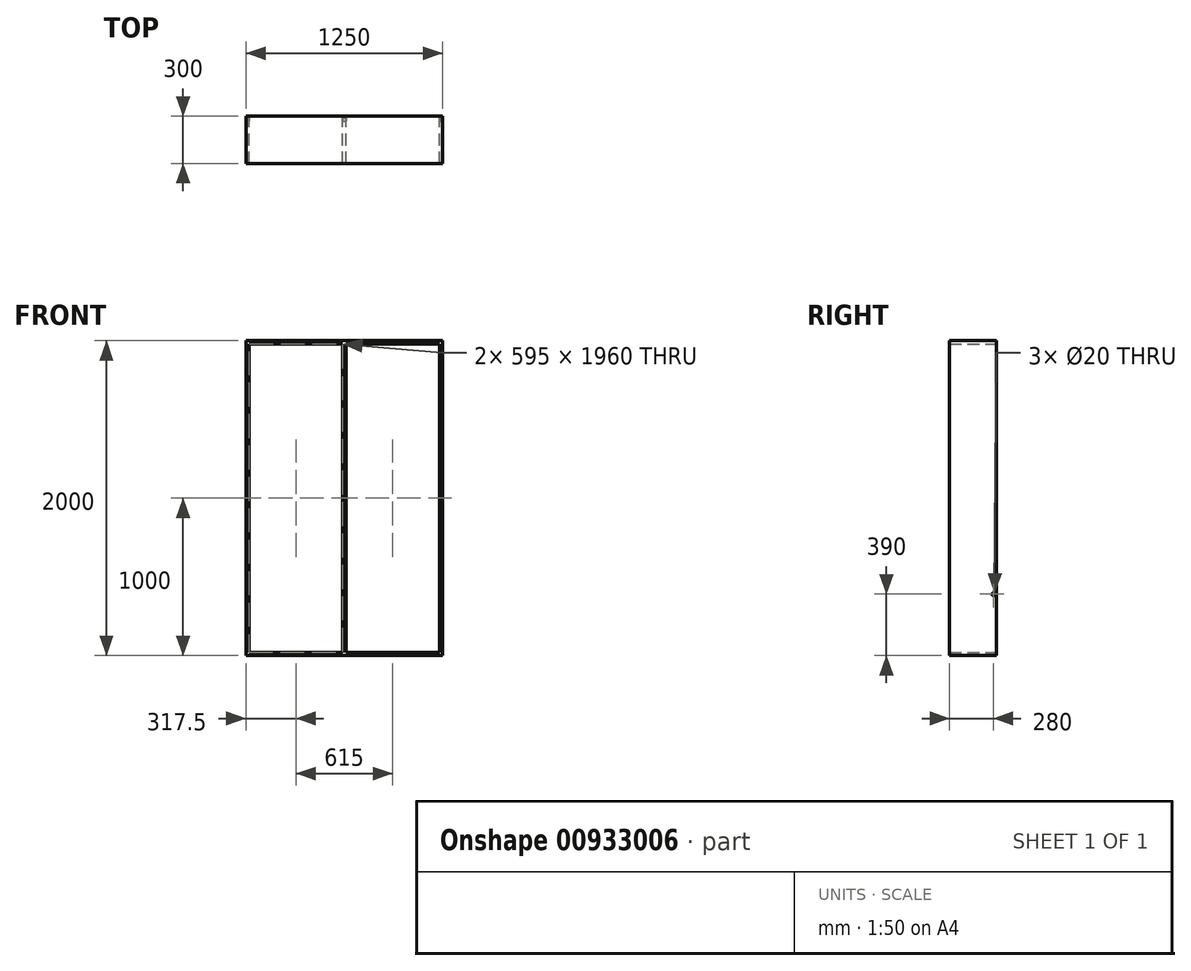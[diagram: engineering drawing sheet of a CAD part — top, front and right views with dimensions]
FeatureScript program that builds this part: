
annotation { "Feature Type Name" : "Feature", "Feature Type Description" : "" }
export const myFeature = defineFeature(function(context is Context, id is Id, definition is map)
    precondition{}
    {
        {
            var Q0;
            Q0=qCreatedBy(makeId("Front.planeOp"),FACE);
            var sketch = newSketch(context, id + "F0", { "sketchPlane" : qUnion([Q0])});
            skLineSegment(sketch, "E0.bottom", {"start": v(0, 0) * mm, "end": v(-1250, 0) * mm});
            skLineSegment(sketch, "E0.top", {"start": v(0, 2000) * mm, "end": v(-1250, 2000) * mm});
            skLineSegment(sketch, "E0.left", {"start": v(0, 0) * mm, "end": v(0, 2000) * mm});
            skLineSegment(sketch, "E0.right", {"start": v(-1250, 0) * mm, "end": v(-1250, 2000) * mm});
            skLineSegment(sketch, "E1.0", {"start": v(-20, 0) * mm, "end": v(-20, 2000) * mm});
            skLineSegment(sketch, "E2.0", {"start": v(0, 20) * mm, "end": v(-1250, 20) * mm});
            skLineSegment(sketch, "E3.0", {"start": v(-1230, 0) * mm, "end": v(-1230, 2000) * mm});
            skLineSegment(sketch, "E4.0", {"start": v(0, 1980) * mm, "end": v(-1250, 1980) * mm});
            skLineSegment(sketch, "E5.0", {"start": v(-635, 1980) * mm, "end": v(-635, 20) * mm});
            skLineSegment(sketch, "E6.0", {"start": v(-615, 1980) * mm, "end": v(-615, 20) * mm});
            skSolve(sketch);
        }
        {
            var Q0;
            Q0 = qSketchRegion(id + "F0", true);
            var Q1;
            {var subQ0=sQuery(id+"F0.wireOp",EDGE,"E5.0");Q1=makeQuery(id+"F0.imprint","IMPRINT",FACE,{"disambiguationData":[TD([[makeQuery(id+"F0.imprint","IMPRINT",EDGE,{"derivedFrom":subQ0}),1.0]])]});}
            extrude(context, id + "F1", {"entities" : qUnion([Q0, Q1]), "depth" : 300 * mm, "offsetDistance" : 25 * mm});
        }
        {
            var Q0;
            Q0=makeQuery(id+"F1.opExtrude","SWEPT_FACE",FACE,{"disambiguationData":[OSD([sQuery(id+"F0.wireOp",EDGE,"E0.left")])]});
            var sketch = newSketch(context, id + "F2", { "sketchPlane" : qUnion([Q0])});
            skLineSegment(sketch, "E7", {"start": v(0, 0) * mm, "end": v(-20, 0) * mm});
            skLineSegment(sketch, "E8", {"start": v(-20, 0) * mm, "end": v(-20, 390) * mm});
            skCircle(sketch, "E9", {"center": v(-20, 390) * mm, "radius": 10 * mm});
            skSolve(sketch);
        }
        {
            var Q0;
            Q0 = qSketchRegion(id + "F2", true);
            extrude(context, id + "F3", {"entities" : qUnion([Q0]), "operationType" : NewBodyOperationType.REMOVE, "endBound" : BoundingType.THROUGH_ALL, "oppositeDirection" : true, "depth" : 25 * mm, "offsetDistance" : 25 * mm});
        }
    });
